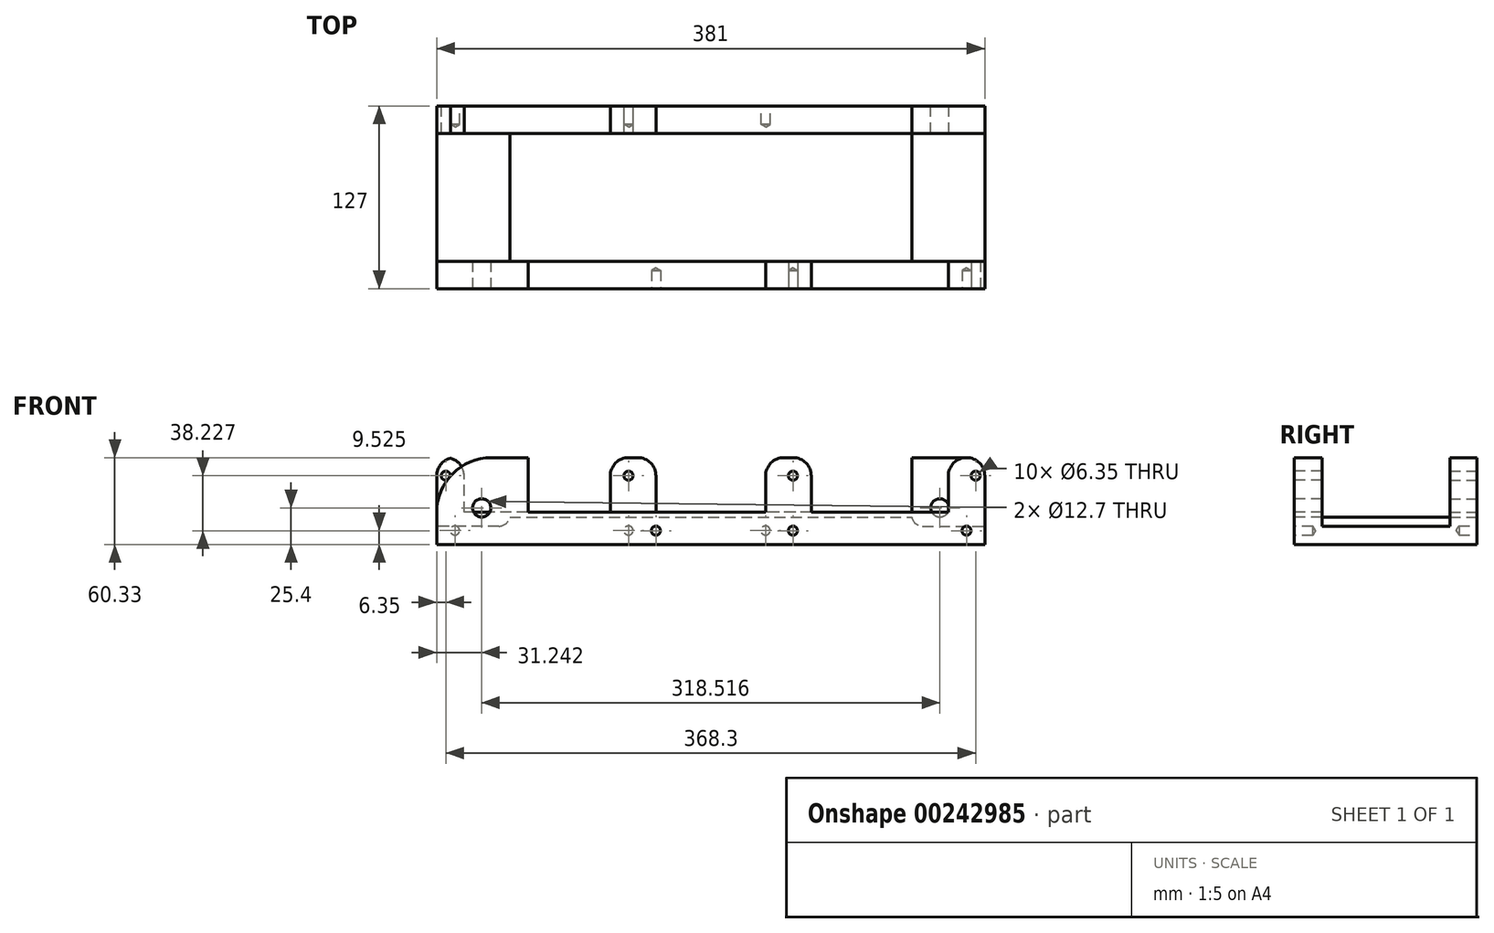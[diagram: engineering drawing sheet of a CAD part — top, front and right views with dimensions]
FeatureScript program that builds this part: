
annotation { "Feature Type Name" : "Feature", "Feature Type Description" : "" }
export const myFeature = defineFeature(function(context is Context, id is Id, definition is map)
    precondition{}
    {
        {
            var Q0;
            Q0=qCreatedBy(makeId("Top.planeOp"),FACE);
            var sketch = newSketch(context, id + "F0", { "sketchPlane" : qUnion([Q0])});
            skLineSegment(sketch, "E0.bottom", {"start": v(190.5, 63.5) * mm, "end": v(-190.5, 63.5) * mm});
            skLineSegment(sketch, "E0.top", {"start": v(190.5, -63.5) * mm, "end": v(-190.5, -63.5) * mm});
            skLineSegment(sketch, "E0.left", {"start": v(190.5, 63.5) * mm, "end": v(190.5, -63.5) * mm});
            skLineSegment(sketch, "E0.right", {"start": v(-190.5, 63.5) * mm, "end": v(-190.5, -63.5) * mm});
            skPoint(sketch, "E0.middle", {"position": v(0, 0) * mm});
            skSolve(sketch);
        }
        {
            var Q0;
            Q0 = qSketchRegion(id + "F0", true);
            extrude(context, id + "F1", {"entities" : qUnion([Q0]), "depth" : 60.32 * mm});
        }
        {
            var Q0;
            Q0=makeQuery(id+"F1.opExtrude","SWEPT_FACE",FACE,{"disambiguationData":[OSD([sQuery(id+"F0.wireOp",EDGE,"E0.left")])]});
            var sketch = newSketch(context, id + "F2", { "sketchPlane" : qUnion([Q0])});
            skLineSegment(sketch, "E1.bottom", {"start": v(-44.45, 60.33) * mm, "end": v(44.45, 60.33) * mm});
            skLineSegment(sketch, "E1.top", {"start": v(-44.45, 19.05) * mm, "end": v(44.45, 19.05) * mm});
            skLineSegment(sketch, "E1.left", {"start": v(-44.45, 60.33) * mm, "end": v(-44.45, 19.05) * mm});
            skLineSegment(sketch, "E1.right", {"start": v(44.45, 60.33) * mm, "end": v(44.45, 19.05) * mm});
            skSolve(sketch);
        }
        {
            var Q0;
            Q0 = qSketchRegion(id + "F2", true);
            var Q1;
            Q1=makeQuery(id+"F1.opExtrude","SWEPT_FACE",FACE,{"disambiguationData":[OSD([sQuery(id+"F0.wireOp",EDGE,"E0.right")])]});
            extrude(context, id + "F3", {"entities" : qUnion([Q0]), "operationType" : NewBodyOperationType.REMOVE, "endBound" : BoundingType.UP_TO_SURFACE, "oppositeDirection" : true, "endBoundEntityFace" : qUnion([Q1]), "depth" : 25.4 * mm});
        }
        {
            var Q0;
            Q0=makeQuery(id+"F1.opExtrude","SWEPT_FACE",FACE,{"disambiguationData":[OSD([sQuery(id+"F0.wireOp",EDGE,"E0.left")])]});
            var sketch = newSketch(context, id + "F4", { "sketchPlane" : qUnion([Q0])});
            skLineSegment(sketch, "E2.bottom", {"start": v(-44.45, 19.05) * mm, "end": v(44.45, 19.05) * mm});
            skLineSegment(sketch, "E2.top", {"start": v(-44.45, 12.7) * mm, "end": v(44.45, 12.7) * mm});
            skLineSegment(sketch, "E2.left", {"start": v(-44.45, 19.05) * mm, "end": v(-44.45, 12.7) * mm});
            skLineSegment(sketch, "E2.right", {"start": v(44.45, 19.05) * mm, "end": v(44.45, 12.7) * mm});
            skSolve(sketch);
        }
        {
            var Q0;
            Q0 = qSketchRegion(id + "F4", true);
            extrude(context, id + "F5", {"entities" : qUnion([Q0]), "operationType" : NewBodyOperationType.REMOVE, "oppositeDirection" : true, "depth" : 50.8 * mm});
        }
        {
            var Q0;
            Q0=makeQuery(id+"F5.boolean.opBoolean","COPY",EDGE,{"derivedFrom":makeQuery(id+"F5.opExtrude","CAP_EDGE",EDGE,{"disambiguationData":[OSD([sQuery(id+"F4.wireOp",EDGE,"E2.top")])],"isStart":false})});
            fillet(context, id + "F6", {"entities" : qUnion([Q0]), "radius" : 7.62 * mm, "tangentPropagation" : true, "allowEdgeOverflow" : false});
        }
        {
            var Q0;
            Q0=makeQuery(id+"F1.opExtrude","SWEPT_FACE",FACE,{"disambiguationData":[OSD([sQuery(id+"F0.wireOp",EDGE,"E0.right")])]});
            var sketch = newSketch(context, id + "F7", { "sketchPlane" : qUnion([Q0])});
            skLineSegment(sketch, "E3.bottom", {"start": v(-44.45, 19.05) * mm, "end": v(44.45, 19.05) * mm});
            skLineSegment(sketch, "E3.top", {"start": v(-44.45, 12.7) * mm, "end": v(44.45, 12.7) * mm});
            skLineSegment(sketch, "E3.left", {"start": v(-44.45, 19.05) * mm, "end": v(-44.45, 12.7) * mm});
            skLineSegment(sketch, "E3.right", {"start": v(44.45, 19.05) * mm, "end": v(44.45, 12.7) * mm});
            skSolve(sketch);
        }
        {
            var Q0;
            Q0 = qSketchRegion(id + "F7", true);
            extrude(context, id + "F8", {"entities" : qUnion([Q0]), "operationType" : NewBodyOperationType.REMOVE, "oppositeDirection" : true, "depth" : 50.8 * mm});
        }
        {
            var Q0;
            Q0=makeQuery(id+"F8.boolean.opBoolean","COPY",EDGE,{"derivedFrom":makeQuery(id+"F8.opExtrude","CAP_EDGE",EDGE,{"disambiguationData":[OSD([sQuery(id+"F7.wireOp",EDGE,"E3.top")])],"isStart":false})});
            fillet(context, id + "F9", {"entities" : qUnion([Q0]), "radius" : 7.62 * mm, "tangentPropagation" : true, "allowEdgeOverflow" : false});
        }
        {
            var Q0;
            Q0=makeQuery(id+"F1.opExtrude","SWEPT_FACE",FACE,{"disambiguationData":[OSD([sQuery(id+"F0.wireOp",EDGE,"E0.top")])]});
            var sketch = newSketch(context, id + "F10", { "sketchPlane" : qUnion([Q0])});
            skLineSegment(sketch, "E4", {"start": v(165.1, 60.33) * mm, "end": v(165.1, 22.35) * mm});
            skLineSegment(sketch, "E5", {"start": v(165.1, 22.35) * mm, "end": v(69.85, 22.35) * mm});
            skLineSegment(sketch, "E6", {"start": v(69.85, 22.35) * mm, "end": v(69.85, 60.33) * mm});
            skLineSegment(sketch, "E7", {"start": v(69.85, 60.33) * mm, "end": v(38.1, 60.33) * mm});
            skLineSegment(sketch, "E8", {"start": v(38.1, 60.33) * mm, "end": v(38.1, 22.35) * mm});
            skLineSegment(sketch, "E9", {"start": v(38.1, 22.35) * mm, "end": v(-127, 22.35) * mm});
            skLineSegment(sketch, "E10", {"start": v(-127, 22.35) * mm, "end": v(-127, 60.33) * mm});
            skLineSegment(sketch, "E11", {"start": v(-127, 60.33) * mm, "end": v(38.1, 60.33) * mm});
            skLineSegment(sketch, "E12", {"start": v(69.85, 60.33) * mm, "end": v(165.1, 60.33) * mm});
            skSolve(sketch);
        }
        {
            var Q0;
            Q0 = qSketchRegion(id + "F10", true);
            var Q1;
            Q1=makeQuery(id+"F8.boolean.opBoolean","MERGE",FACE,{"derivedFrom":[makeQuery(id+"F5.boolean.opBoolean","MERGE",FACE,{"derivedFrom":[makeQuery(id+"F3.boolean.opBoolean","COPY",FACE,{"derivedFrom":makeQuery(id+"F3.opExtrude","SWEPT_FACE",FACE,{"disambiguationData":[OSD([sQuery(id+"F2.wireOp",EDGE,"E1.left")])]})}),makeQuery(id+"F5.opExtrude","SWEPT_FACE",FACE,{"disambiguationData":[OSD([sQuery(id+"F4.wireOp",EDGE,"E2.left")])]})]}),makeQuery(id+"F8.opExtrude","SWEPT_FACE",FACE,{"disambiguationData":[OSD([sQuery(id+"F7.wireOp",EDGE,"E3.right")])]})]});
            extrude(context, id + "F11", {"entities" : qUnion([Q0]), "operationType" : NewBodyOperationType.REMOVE, "endBound" : BoundingType.UP_TO_SURFACE, "oppositeDirection" : true, "endBoundEntityFace" : qUnion([Q1]), "depth" : 25.4 * mm});
        }
        {
            var Q0;
            Q0=makeQuery(id+"F1.opExtrude","SWEPT_FACE",FACE,{"disambiguationData":[OSD([sQuery(id+"F0.wireOp",EDGE,"E0.bottom")])]});
            var sketch = newSketch(context, id + "F12", { "sketchPlane" : qUnion([Q0])});
            skLineSegment(sketch, "E13", {"start": v(-139.7, 60.33) * mm, "end": v(-139.7, 22.35) * mm});
            skLineSegment(sketch, "E14", {"start": v(-139.7, 22.35) * mm, "end": v(38.1, 22.35) * mm});
            skLineSegment(sketch, "E15", {"start": v(38.1, 22.35) * mm, "end": v(38.1, 60.32) * mm});
            skLineSegment(sketch, "E16", {"start": v(38.1, 60.33) * mm, "end": v(69.85, 60.33) * mm});
            skLineSegment(sketch, "E17", {"start": v(69.85, 60.33) * mm, "end": v(69.85, 22.35) * mm});
            skLineSegment(sketch, "E18", {"start": v(69.85, 22.35) * mm, "end": v(171.45, 22.35) * mm});
            skLineSegment(sketch, "E19", {"start": v(171.45, 22.35) * mm, "end": v(171.45, 60.33) * mm});
            skLineSegment(sketch, "E20", {"start": v(171.45, 60.33) * mm, "end": v(69.85, 60.33) * mm});
            skLineSegment(sketch, "E21", {"start": v(38.1, 60.33) * mm, "end": v(-139.7, 60.33) * mm});
            skSolve(sketch);
        }
        {
            var Q0;
            Q0 = qSketchRegion(id + "F12", true);
            var Q1;
            Q1=makeQuery(id+"F8.boolean.opBoolean","MERGE",FACE,{"derivedFrom":[makeQuery(id+"F5.boolean.opBoolean","MERGE",FACE,{"derivedFrom":[makeQuery(id+"F3.boolean.opBoolean","COPY",FACE,{"derivedFrom":makeQuery(id+"F3.opExtrude","SWEPT_FACE",FACE,{"disambiguationData":[OSD([sQuery(id+"F2.wireOp",EDGE,"E1.right")])]})}),makeQuery(id+"F5.opExtrude","SWEPT_FACE",FACE,{"disambiguationData":[OSD([sQuery(id+"F4.wireOp",EDGE,"E2.right")])]})]}),makeQuery(id+"F8.opExtrude","SWEPT_FACE",FACE,{"disambiguationData":[OSD([sQuery(id+"F7.wireOp",EDGE,"E3.left")])]})]});
            extrude(context, id + "F13", {"entities" : qUnion([Q0]), "operationType" : NewBodyOperationType.REMOVE, "endBound" : BoundingType.UP_TO_SURFACE, "oppositeDirection" : true, "endBoundEntityFace" : qUnion([Q1]), "depth" : 25.4 * mm});
        }
        {
            var Q0;
            {var subQ0=sQuery(id+"F0.wireOp",EDGE,"E0.right");var subQ1=sQuery(id+"F0.wireOp",EDGE,"E0.top");Q0=makeQuery(id+"F3.boolean.opBoolean","SPLIT",EDGE,{"disambiguationData":[TD([makeQuery(id+"F1.opExtrude","SWEPT_FACE",FACE,{"disambiguationData":[OSD([subQ1])]})])],"derivedFrom":makeQuery(id+"F1.opExtrude","CAP_EDGE",EDGE,{"disambiguationData":[OSD([subQ0])],"isStart":false})});}
            fillet(context, id + "F14", {"entities" : qUnion([Q0]), "radius" : 38.1 * mm, "tangentPropagation" : true, "allowEdgeOverflow" : false});
        }
        {
            var Q0;
            Q0=makeQuery(id+"F11.boolean.opBoolean","COPY",EDGE,{"derivedFrom":makeQuery(id+"F11.opExtrude","SWEPT_EDGE",EDGE,{"disambiguationData":[OSD([sQuery(id+"F0.wireOp",EDGE,"E0.top"),sQuery(id+"F10.wireOp",EDGE,"E10"),sQuery(id+"F10.wireOp",EDGE,"E11")])]})});
            var Q1;
            Q1=makeQuery(id+"F11.boolean.opBoolean","COPY",EDGE,{"derivedFrom":makeQuery(id+"F11.opExtrude","SWEPT_EDGE",EDGE,{"disambiguationData":[OSD([sQuery(id+"F10.wireOp",EDGE,"E7"),sQuery(id+"F10.wireOp",EDGE,"E8"),sQuery(id+"F10.wireOp",EDGE,"E11")])]})});
            var Q2;
            Q2=makeQuery(id+"F11.boolean.opBoolean","COPY",EDGE,{"derivedFrom":makeQuery(id+"F11.opExtrude","SWEPT_EDGE",EDGE,{"disambiguationData":[OSD([sQuery(id+"F10.wireOp",EDGE,"E6"),sQuery(id+"F10.wireOp",EDGE,"E7"),sQuery(id+"F10.wireOp",EDGE,"E12")])]})});
            var Q3;
            Q3=makeQuery(id+"F11.boolean.opBoolean","COPY",EDGE,{"derivedFrom":makeQuery(id+"F11.opExtrude","SWEPT_EDGE",EDGE,{"disambiguationData":[OSD([sQuery(id+"F0.wireOp",EDGE,"E0.top"),sQuery(id+"F10.wireOp",EDGE,"E4"),sQuery(id+"F10.wireOp",EDGE,"E12")])]})});
            var Q4;
            {var subQ0=sQuery(id+"F0.wireOp",EDGE,"E0.left");var subQ1=sQuery(id+"F0.wireOp",EDGE,"E0.top");Q4=makeQuery(id+"F3.boolean.opBoolean","SPLIT",EDGE,{"disambiguationData":[TD([makeQuery(id+"F1.opExtrude","SWEPT_FACE",FACE,{"disambiguationData":[OSD([subQ1])]})])],"derivedFrom":makeQuery(id+"F1.opExtrude","CAP_EDGE",EDGE,{"disambiguationData":[OSD([subQ0])],"isStart":false})});}
            fillet(context, id + "F15", {"entities" : qUnion([Q0, Q1, Q2, Q3, Q4]), "radius" : 12.7 * mm, "tangentPropagation" : true, "allowEdgeOverflow" : false});
        }
        {
            var Q0;
            Q0=makeQuery(id+"F13.boolean.opBoolean","COPY",EDGE,{"derivedFrom":makeQuery(id+"F13.opExtrude","SWEPT_EDGE",EDGE,{"disambiguationData":[OSD([sQuery(id+"F0.wireOp",EDGE,"E0.bottom"),sQuery(id+"F12.wireOp",EDGE,"E19"),sQuery(id+"F12.wireOp",EDGE,"E20")])]})});
            var Q1;
            {var subQ0=sQuery(id+"F0.wireOp",EDGE,"E0.bottom");var subQ1=sQuery(id+"F0.wireOp",EDGE,"E0.right");Q1=makeQuery(id+"F3.boolean.opBoolean","SPLIT",EDGE,{"disambiguationData":[TD([makeQuery(id+"F1.opExtrude","SWEPT_FACE",FACE,{"disambiguationData":[OSD([subQ0])]})])],"derivedFrom":makeQuery(id+"F1.opExtrude","CAP_EDGE",EDGE,{"disambiguationData":[OSD([subQ1])],"isStart":false})});}
            var Q2;
            Q2=makeQuery(id+"F13.boolean.opBoolean","COPY",EDGE,{"derivedFrom":makeQuery(id+"F13.opExtrude","SWEPT_EDGE",EDGE,{"disambiguationData":[OSD([sQuery(id+"F12.wireOp",EDGE,"E16"),sQuery(id+"F12.wireOp",EDGE,"E17"),sQuery(id+"F12.wireOp",EDGE,"E20")])]})});
            var Q3;
            Q3=makeQuery(id+"F13.boolean.opBoolean","COPY",EDGE,{"derivedFrom":makeQuery(id+"F13.opExtrude","SWEPT_EDGE",EDGE,{"disambiguationData":[OSD([sQuery(id+"F12.wireOp",EDGE,"E15"),sQuery(id+"F12.wireOp",EDGE,"E16"),sQuery(id+"F12.wireOp",EDGE,"E21")])]})});
            var Q4;
            Q4=makeQuery(id+"F13.boolean.opBoolean","COPY",EDGE,{"derivedFrom":makeQuery(id+"F13.opExtrude","SWEPT_EDGE",EDGE,{"disambiguationData":[OSD([sQuery(id+"F0.wireOp",EDGE,"E0.bottom"),sQuery(id+"F12.wireOp",EDGE,"E13"),sQuery(id+"F12.wireOp",EDGE,"E21")])]})});
            var Q5;
            {var subQ0=sQuery(id+"F0.wireOp",EDGE,"E0.bottom");var subQ1=sQuery(id+"F0.wireOp",EDGE,"E0.left");Q5=makeQuery(id+"F3.boolean.opBoolean","SPLIT",EDGE,{"disambiguationData":[TD([makeQuery(id+"F1.opExtrude","SWEPT_FACE",FACE,{"disambiguationData":[OSD([subQ0])]})])],"derivedFrom":makeQuery(id+"F1.opExtrude","CAP_EDGE",EDGE,{"disambiguationData":[OSD([subQ1])],"isStart":false})});}
            fillet(context, id + "F16", {"entities" : qUnion([Q0, Q1, Q2, Q3, Q4, Q5]), "radius" : 12.7 * mm, "tangentPropagation" : true, "allowEdgeOverflow" : false});
        }
        {
            var Q0;
            Q0=makeQuery(id+"F1.opExtrude","SWEPT_FACE",FACE,{"disambiguationData":[OSD([sQuery(id+"F0.wireOp",EDGE,"E0.top")])]});
            var sketch = newSketch(context, id + "F17", { "sketchPlane" : qUnion([Q0])});
            skPoint(sketch, "E22", {"position": v(184.15, 47.75) * mm});
            skPoint(sketch, "E23", {"position": v(177.8, 9.52) * mm});
            skPoint(sketch, "E24", {"position": v(57.15, 9.53) * mm});
            skPoint(sketch, "E25", {"position": v(57.15, 47.75) * mm});
            skPoint(sketch, "E26", {"position": v(-38.1, 9.53) * mm});
            skPoint(sketch, "E27", {"position": v(-159.26, 25.4) * mm});
            skSolve(sketch);
        }
        {
            var Q0;
            Q0=sQuery(id+"F17.wireOp",VERTEX,"E26");
            var Q1;
            Q1=sQuery(id+"F17.wireOp",VERTEX,"E24");
            var Q2;
            Q2=sQuery(id+"F17.wireOp",VERTEX,"E23");
            var Q3;
            Q3=makeQuery(id+"F1.opExtrude","SWEPT_BODY",BODY,{"disambiguationData":[OSD([sQuery(id+"F0.wireOp",EDGE,"E0.bottom"),sQuery(id+"F0.wireOp",EDGE,"E0.top"),sQuery(id+"F0.wireOp",EDGE,"E0.left"),sQuery(id+"F0.wireOp",EDGE,"E0.right")])]});
            hole(context, id + "F18", {"style" : HoleStyle.SIMPLE, "endStyle" : HoleEndStyle.BLIND, "holeDiameter" : 6.35 * mm, "holeDepth" : 12.7 * mm, "startFromSketch" : true, "locations" : qUnion([Q0, Q1, Q2]), "scope" : qUnion([Q3])});
        }
        {
            var Q0;
            Q0=sQuery(id+"F17.wireOp",VERTEX,"E25");
            var Q1;
            Q1=sQuery(id+"F17.wireOp",VERTEX,"E22");
            var Q2;
            Q2=makeQuery(id+"F1.opExtrude","SWEPT_BODY",BODY,{"disambiguationData":[OSD([sQuery(id+"F0.wireOp",EDGE,"E0.bottom"),sQuery(id+"F0.wireOp",EDGE,"E0.top"),sQuery(id+"F0.wireOp",EDGE,"E0.left"),sQuery(id+"F0.wireOp",EDGE,"E0.right")])]});
            hole(context, id + "F19", {"style" : HoleStyle.SIMPLE, "endStyle" : HoleEndStyle.BLIND, "holeDiameter" : 6.35 * mm, "holeDepth" : 25.4 * mm, "startFromSketch" : true, "locations" : qUnion([Q0, Q1]), "scope" : qUnion([Q2])});
        }
        {
            var Q0;
            Q0=sQuery(id+"F17.wireOp",VERTEX,"E27");
            var Q1;
            Q1=makeQuery(id+"F1.opExtrude","SWEPT_BODY",BODY,{"disambiguationData":[OSD([sQuery(id+"F0.wireOp",EDGE,"E0.bottom"),sQuery(id+"F0.wireOp",EDGE,"E0.top"),sQuery(id+"F0.wireOp",EDGE,"E0.left"),sQuery(id+"F0.wireOp",EDGE,"E0.right")])]});
            hole(context, id + "F20", {"style" : HoleStyle.SIMPLE, "endStyle" : HoleEndStyle.BLIND, "holeDiameter" : 12.7 * mm, "holeDepth" : 25.4 * mm, "startFromSketch" : true, "locations" : qUnion([Q0]), "scope" : qUnion([Q1])});
        }
        {
            var Q0;
            Q0=makeQuery(id+"F1.opExtrude","SWEPT_FACE",FACE,{"disambiguationData":[OSD([sQuery(id+"F0.wireOp",EDGE,"E0.bottom")])]});
            var sketch = newSketch(context, id + "F21", { "sketchPlane" : qUnion([Q0])});
            skPoint(sketch, "E28", {"position": v(184.15, 47.75) * mm});
            skPoint(sketch, "E29", {"position": v(177.8, 9.65) * mm});
            skPoint(sketch, "E30", {"position": v(57.15, 9.65) * mm});
            skPoint(sketch, "E31", {"position": v(57.15, 47.75) * mm});
            skPoint(sketch, "E32", {"position": v(-38.1, 9.65) * mm});
            skPoint(sketch, "E33", {"position": v(-159.26, 25.4) * mm});
            skSolve(sketch);
        }
        {
            var Q0;
            Q0=sQuery(id+"F21.wireOp",VERTEX,"E33");
            var Q1;
            Q1=makeQuery(id+"F1.opExtrude","SWEPT_BODY",BODY,{"disambiguationData":[OSD([sQuery(id+"F0.wireOp",EDGE,"E0.bottom"),sQuery(id+"F0.wireOp",EDGE,"E0.top"),sQuery(id+"F0.wireOp",EDGE,"E0.left"),sQuery(id+"F0.wireOp",EDGE,"E0.right")])]});
            hole(context, id + "F22", {"style" : HoleStyle.SIMPLE, "endStyle" : HoleEndStyle.BLIND, "holeDiameter" : 12.7 * mm, "holeDepth" : 25.4 * mm, "startFromSketch" : true, "locations" : qUnion([Q0]), "scope" : qUnion([Q1])});
        }
        {
            var Q0;
            Q0=sQuery(id+"F21.wireOp",VERTEX,"E32");
            var Q1;
            Q1=sQuery(id+"F21.wireOp",VERTEX,"E30");
            var Q2;
            Q2=sQuery(id+"F21.wireOp",VERTEX,"E29");
            var Q3;
            Q3=makeQuery(id+"F1.opExtrude","SWEPT_BODY",BODY,{"disambiguationData":[OSD([sQuery(id+"F0.wireOp",EDGE,"E0.bottom"),sQuery(id+"F0.wireOp",EDGE,"E0.top"),sQuery(id+"F0.wireOp",EDGE,"E0.left"),sQuery(id+"F0.wireOp",EDGE,"E0.right")])]});
            hole(context, id + "F23", {"style" : HoleStyle.SIMPLE, "endStyle" : HoleEndStyle.BLIND, "holeDiameter" : 6.35 * mm, "holeDepth" : 12.7 * mm, "startFromSketch" : true, "locations" : qUnion([Q0, Q1, Q2]), "scope" : qUnion([Q3])});
        }
        {
            var Q0;
            Q0=sQuery(id+"F21.wireOp",VERTEX,"E31");
            var Q1;
            Q1=sQuery(id+"F21.wireOp",VERTEX,"E28");
            var Q2;
            Q2=makeQuery(id+"F1.opExtrude","SWEPT_BODY",BODY,{"disambiguationData":[OSD([sQuery(id+"F0.wireOp",EDGE,"E0.bottom"),sQuery(id+"F0.wireOp",EDGE,"E0.top"),sQuery(id+"F0.wireOp",EDGE,"E0.left"),sQuery(id+"F0.wireOp",EDGE,"E0.right")])]});
            hole(context, id + "F24", {"style" : HoleStyle.SIMPLE, "endStyle" : HoleEndStyle.BLIND, "holeDiameter" : 6.35 * mm, "holeDepth" : 25.4 * mm, "startFromSketch" : true, "locations" : qUnion([Q0, Q1]), "scope" : qUnion([Q2])});
        }
    });
